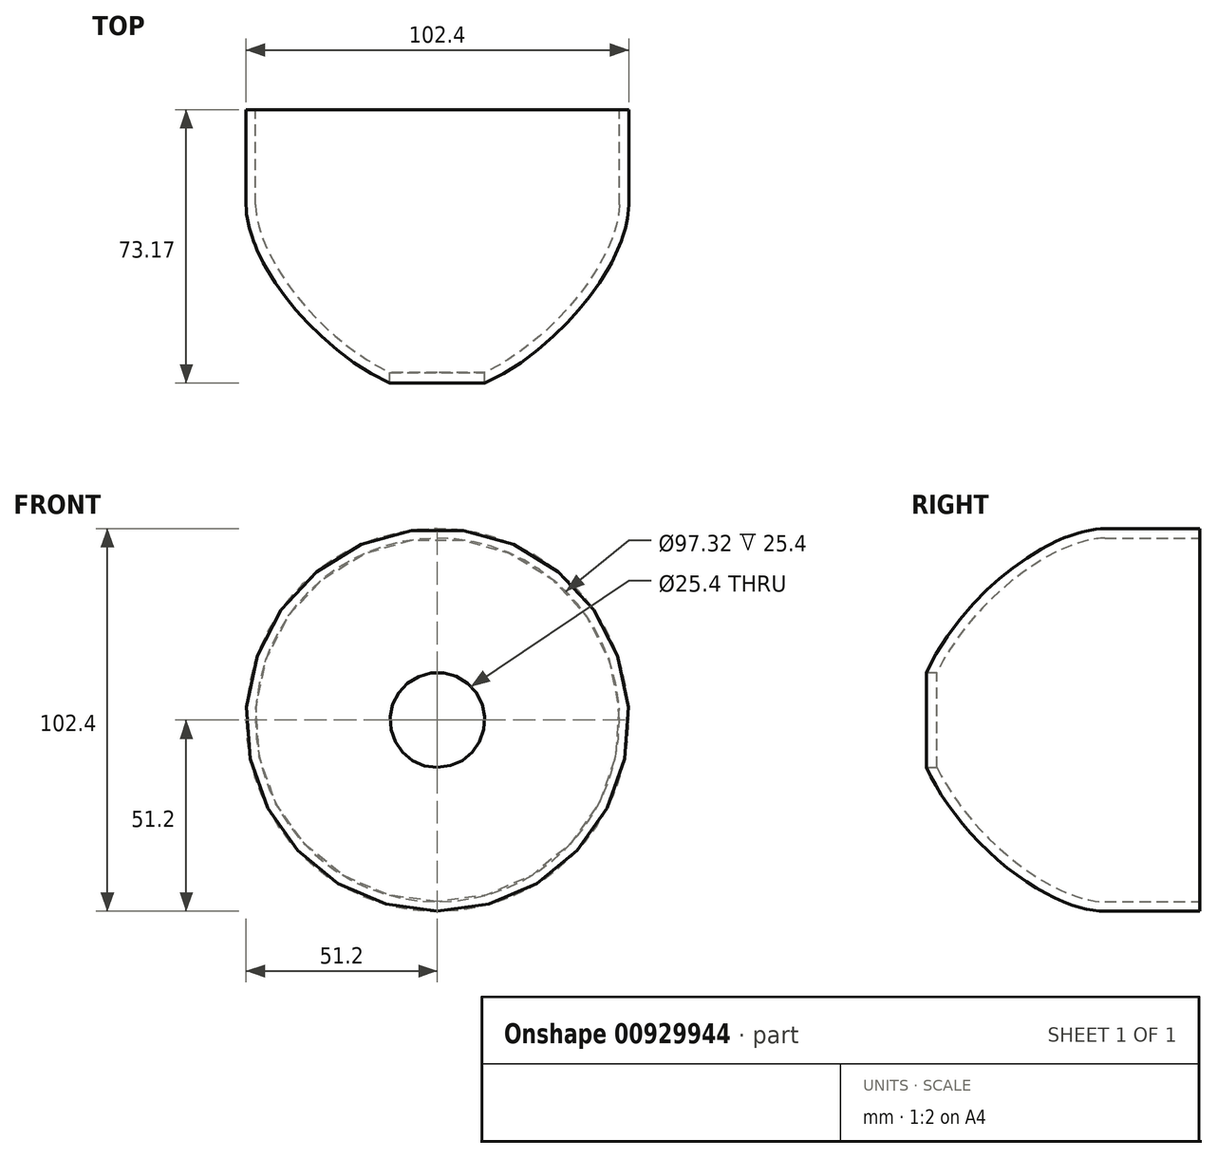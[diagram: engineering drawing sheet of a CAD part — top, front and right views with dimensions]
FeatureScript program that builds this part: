
annotation { "Feature Type Name" : "Feature", "Feature Type Description" : "" }
export const myFeature = defineFeature(function(context is Context, id is Id, definition is map)
    precondition{}
    {
        {
            var Q0;
            Q0=qCreatedBy(makeId("Front.planeOp"),FACE);
            var sketch = newSketch(context, id + "F0", { "sketchPlane" : qUnion([Q0])});
            skCircle(sketch, "E0", {"center": v(0, 0) * mm, "radius": 51.2 * mm});
            skSolve(sketch);
        }
        {
            var Q0;
            Q0=makeQuery(id+"F0.imprint","IMPRINT",FACE,{"disambiguationData":[TD([[makeQuery(id+"F0.imprint","IMPRINT",EDGE,{"derivedFrom":sQuery(id+"F0.wireOp",EDGE,"E0")}),1.0]])]});
            extrude(context, id + "F1", {"entities" : qUnion([Q0]), "depth" : 76.2 * mm, "offsetDistance" : 25.4 * mm});
        }
        {
            var Q0;
            Q0=makeQuery(id+"F1.opExtrude","CAP_EDGE",EDGE,{"disambiguationData":[OSD([sQuery(id+"F0.wireOp",EDGE,"E0")])],"isStart":false});
            fillet(context, id + "F2", {"entities" : qUnion([Q0]), "radius" : 50.8 * mm, "tangentPropagation" : true, "rho" : 0.3, "crossSection" : FilletCrossSection.CONIC, "allowEdgeOverflow" : false});
        }
        {
            var Q0;
            Q0=qCreatedBy(makeId("Front.planeOp"),FACE);
            var sketch = newSketch(context, id + "F3", { "sketchPlane" : qUnion([Q0])});
            skCircle(sketch, "E1", {"center": v(0, 0) * mm, "radius": 52.38 * mm});
            skSolve(sketch);
        }
        {
            var Q0;
            Q0=makeQuery(id+"F1.opExtrude","CAP_FACE",FACE,{"disambiguationData":[OSD([sQuery(id+"F0.wireOp",EDGE,"E0")])],"isStart":true});
            shell(context, id + "F4", {"entities" : qUnion([Q0]), "thickness" : 2.54 * mm});
        }
        {
            var Q0;
            Q0=sQuery(id+"F3.wireOp",VERTEX,"E1.center");
            var Q1;
            Q1=makeQuery(id+"F1.opExtrude","SWEPT_BODY",BODY,{"disambiguationData":[OSD([sQuery(id+"F0.wireOp",EDGE,"E0")])]});
            hole(context, id + "F5", {"style" : HoleStyle.SIMPLE, "endStyle" : HoleEndStyle.THROUGH, "oppositeDirection" : true, "holeDiameter" : 25.4 * mm, "majorDiameter" : 6.35 * mm, "isTappedThrough" : true, "tappedDepth" : 12.7 * mm, "tapClearance" : 3, "locations" : qUnion([Q0]), "scope" : qUnion([Q1])});
        }
    });
